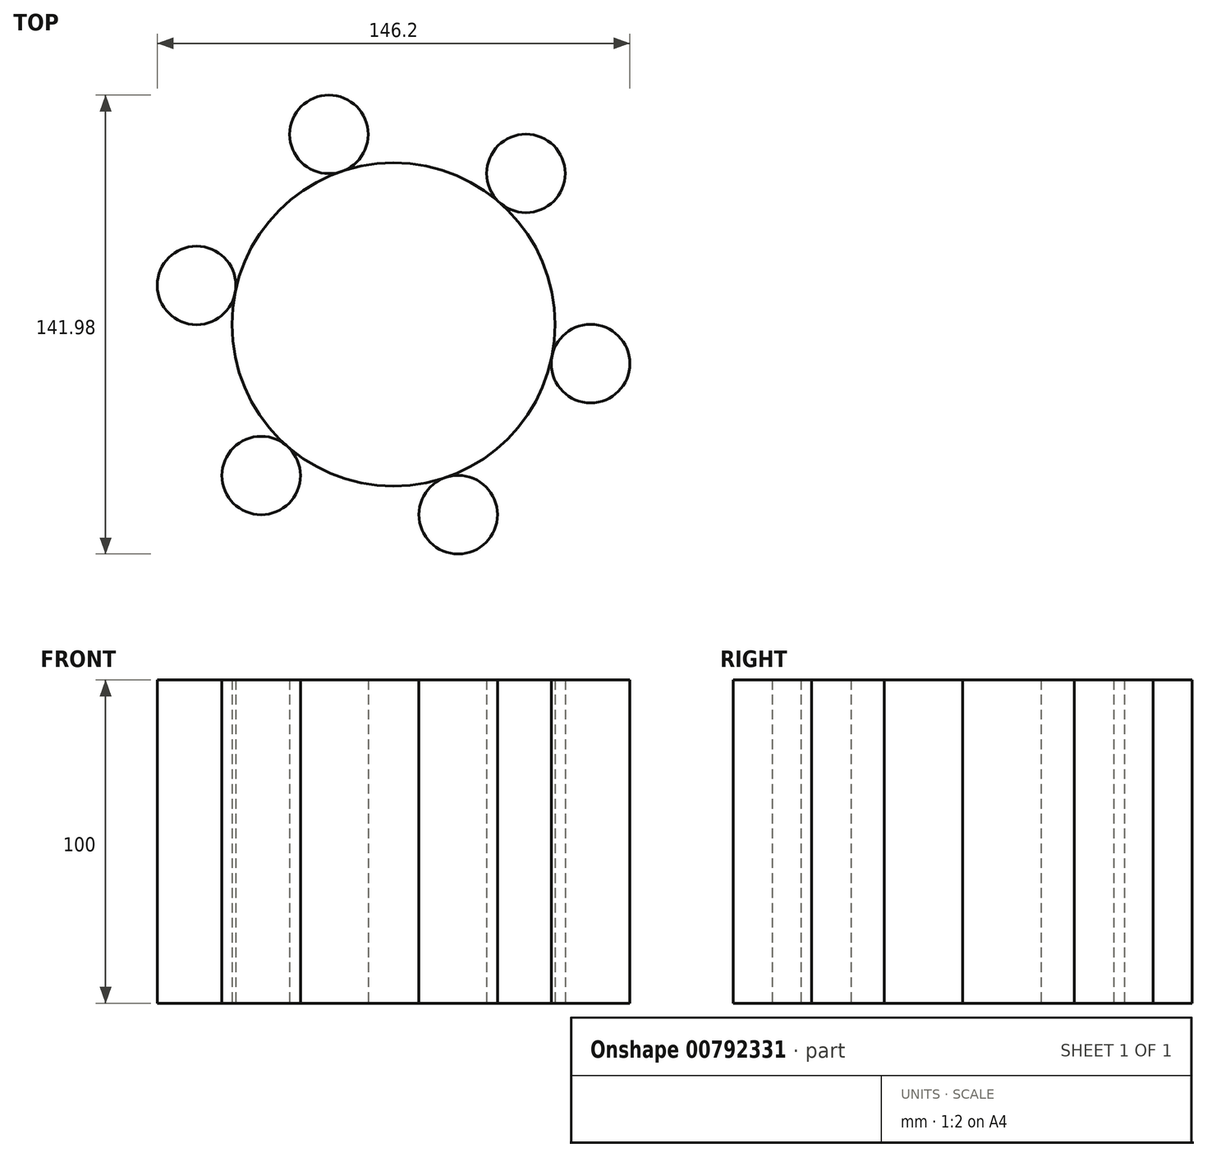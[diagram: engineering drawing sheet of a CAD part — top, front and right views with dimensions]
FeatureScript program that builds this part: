
annotation { "Feature Type Name" : "Feature", "Feature Type Description" : "" }
export const myFeature = defineFeature(function(context is Context, id is Id, definition is map)
    precondition{}
    {
        {
            var Q0;
            Q0=qCreatedBy(makeId("Top.planeOp"),FACE);
            var sketch = newSketch(context, id + "F0", { "sketchPlane" : qUnion([Q0])});
            skCircle(sketch, "E0", {"center": v(0, 0) * mm, "radius": 50 * mm});
            skCircle(sketch, "E1", {"center": v(-60.96, 12.1) * mm, "radius": 12.15 * mm});
            skSolve(sketch);
        }
        {
            var Q0;
            Q0=makeQuery(id+"F0.imprint","IMPRINT",FACE,{"disambiguationData":[TD([[makeQuery(id+"F0.imprint","IMPRINT",EDGE,{"derivedFrom":sQuery(id+"F0.wireOp",EDGE,"E1")}),1.0]])]});
            var Q1;
            Q1=makeQuery(id+"F0.imprint","IMPRINT",FACE,{"disambiguationData":[TD([[makeQuery(id+"F0.imprint","IMPRINT",EDGE,{"derivedFrom":sQuery(id+"F0.wireOp",EDGE,"E0")}),1.0]])]});
            extrude(context, id + "F1", {"entities" : qUnion([Q0, Q1]), "endBound" : BoundingType.SYMMETRIC, "depth" : 100 * mm, "offsetDistance" : 25 * mm});
        }
        {
            var Q0;
            Q0=makeQuery(id+"F1.opExtrude","SWEPT_BODY",BODY,{"disambiguationData":[OSD([sQuery(id+"F0.wireOp",EDGE,"E1")])]});
            var Q1;
            Q1=makeQuery(id+"F1.opExtrude","SWEPT_FACE",FACE,{"disambiguationData":[OSD([sQuery(id+"F0.wireOp",EDGE,"E0")])]});
            circularPattern(context, id + "F2", {"entities" : qUnion([Q0]), "axis" : qUnion([Q1]), "angle" : 360 * degree, "instanceCount" : 6, "equalSpace" : true});
        }
    });
